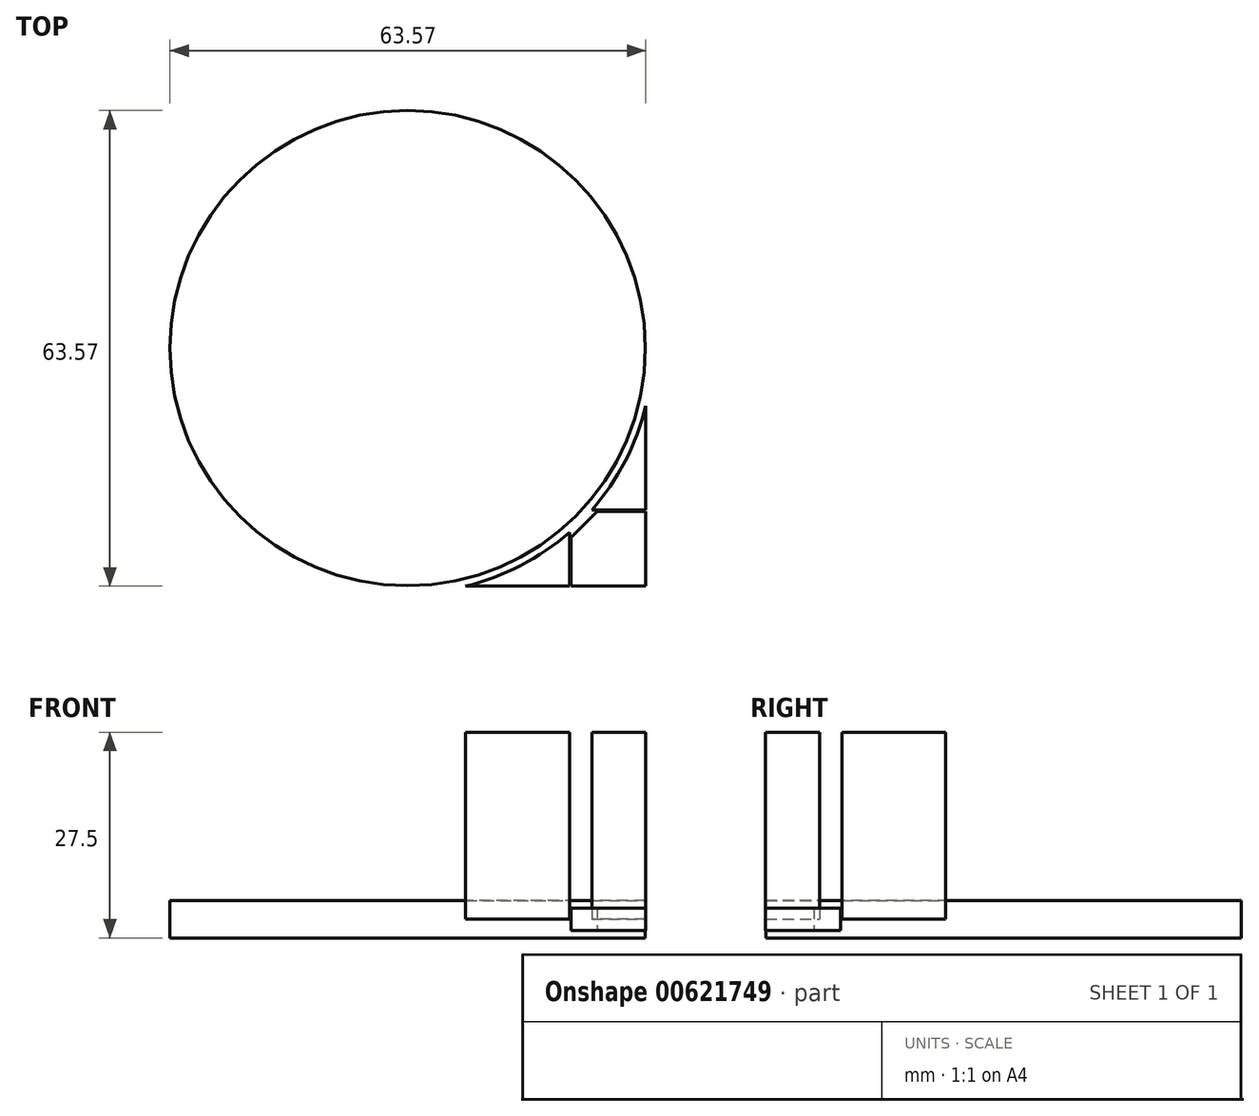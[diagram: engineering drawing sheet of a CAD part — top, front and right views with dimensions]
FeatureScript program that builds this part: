
annotation { "Feature Type Name" : "Feature", "Feature Type Description" : "" }
export const myFeature = defineFeature(function(context is Context, id is Id, definition is map)
    precondition{}
    {
        {
            var Q0;
            Q0=qCreatedBy(makeId("Top.planeOp"),FACE);
            var sketch = newSketch(context, id + "F0", { "sketchPlane" : qUnion([Q0])});
            skLineSegment(sketch, "E0", {"start": v(0, 0) * mm, "end": v(-31.82, 31.82) * mm, "construction": true});
            skCircle(sketch, "E1", {"center": v(-31.82, 31.82) * mm, "radius": 31.75 * mm});
            skSolve(sketch);
        }
        {
            var Q0;
            Q0=makeQuery(id+"F0.imprint","IMPRINT",FACE,{"disambiguationData":[TD([[makeQuery(id+"F0.imprint","IMPRINT",EDGE,{"derivedFrom":sQuery(id+"F0.wireOp",EDGE,"E1")}),1.0]])]});
            extrude(context, id + "F1", {"entities" : qUnion([Q0]), "depth" : 5 * mm, "offsetDistance" : 25 * mm, "symmetric" : true});
        }
        {
            var Q0;
            Q0=qCreatedBy(makeId("Top.planeOp"),FACE);
            var sketch = newSketch(context, id + "F2", { "sketchPlane" : qUnion([Q0])});
            skArc(sketch, "E2.0", {"start": v(-24.07, 0) * mm, "mid": v(-16.7, 2.77) * mm, "end": v(-10.2, 7.22) * mm});
            skLineSegment(sketch, "E3", {"start": v(0, 0) * mm, "end": v(0, 10) * mm});
            skLineSegment(sketch, "E4", {"start": v(0, 0) * mm, "end": v(-10, 0) * mm});
            skLineSegment(sketch, "E5.top", {"start": v(0, 10) * mm, "end": v(-6.47, 10) * mm});
            skLineSegment(sketch, "E5.right", {"start": v(-10, 0) * mm, "end": v(-10, 6.47) * mm});
            skLineSegment(sketch, "E6", {"start": v(-10, 6.47) * mm, "end": v(-6.47, 10) * mm});
            skLineSegment(sketch, "E7.trimOffspring", {"start": v(-10.2, 0) * mm, "end": v(-24.07, 0) * mm});
            skLineSegment(sketch, "E8.trimOffspring", {"start": v(0, 10.2) * mm, "end": v(0, 24.07) * mm});
            skArc(sketch, "E9.trimOffspring", {"start": v(-7.22, 10.2) * mm, "mid": v(-2.77, 16.7) * mm, "end": v(0, 24.07) * mm});
            skLineSegment(sketch, "E10", {"start": v(-10.2, 0) * mm, "end": v(-10.2, 7.22) * mm});
            skLineSegment(sketch, "E11", {"start": v(0, 10.2) * mm, "end": v(-7.22, 10.2) * mm});
            skSolve(sketch);
        }
        {
            var Q0;
            Q0=makeQuery(id+"F2.imprint","IMPRINT",FACE,{"disambiguationData":[TD([[makeQuery(id+"F2.imprint","IMPRINT",EDGE,{"derivedFrom":sQuery(id+"F2.wireOp",EDGE,"E4")}),-1.0]])]});
            extrude(context, id + "F3", {"entities" : qUnion([Q0]), "depth" : 3 * mm, "offsetDistance" : 25 * mm, "symmetric" : true});
        }
        {
            var Q0;
            Q0=makeQuery(id+"F2.imprint","IMPRINT",FACE,{"disambiguationData":[TD([[makeQuery(id+"F2.imprint","IMPRINT",EDGE,{"derivedFrom":sQuery(id+"F2.wireOp",EDGE,"E2.0")}),-1.0]])]});
            var Q1;
            Q1=makeQuery(id+"F2.imprint","IMPRINT",FACE,{"disambiguationData":[TD([[makeQuery(id+"F2.imprint","IMPRINT",EDGE,{"derivedFrom":sQuery(id+"F2.wireOp",EDGE,"E8.trimOffspring")}),1.0]])]});
            extrude(context, id + "F4", {"entities" : qUnion([Q0, Q1]), "depth" : 25 * mm, "offsetDistance" : 25 * mm});
        }
    });
